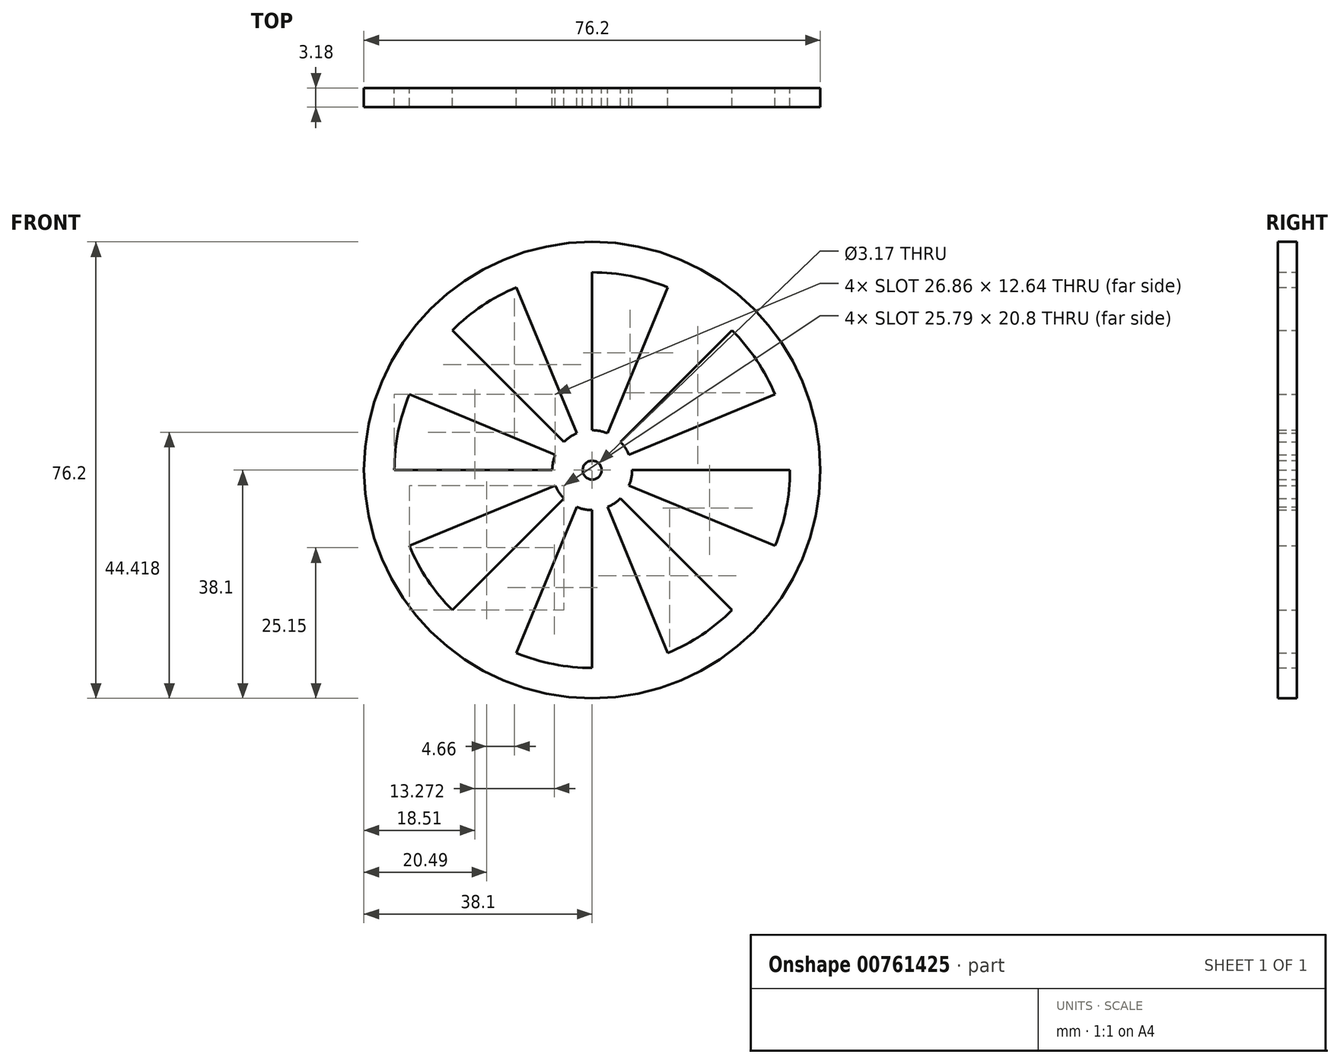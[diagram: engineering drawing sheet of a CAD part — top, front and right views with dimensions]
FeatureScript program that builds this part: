
annotation { "Feature Type Name" : "Feature", "Feature Type Description" : "" }
export const myFeature = defineFeature(function(context is Context, id is Id, definition is map)
    precondition{}
    {
        {
            var Q0;
            Q0=qCreatedBy(makeId("Front.planeOp"),FACE);
            var sketch = newSketch(context, id + "F0", { "sketchPlane" : qUnion([Q0])});
            skCircle(sketch, "E0", {"center": v(0, 0) * mm, "radius": 38.1 * mm});
            skCircle(sketch, "E1", {"center": v(0, 0) * mm, "radius": 33.02 * mm});
            skCircle(sketch, "E2", {"center": v(0, 0) * mm, "radius": 1.59 * mm});
            skCircle(sketch, "E3", {"center": v(0, 0) * mm, "radius": 6.67 * mm});
            skLineSegment(sketch, "E4", {"start": v(0, -33.02) * mm, "end": v(0, -6.67) * mm});
            skLineSegment(sketch, "E5", {"start": v(-12.64, -30.5) * mm, "end": v(-2.55, -6.16) * mm});
            skLineSegment(sketch, "E6.1.0", {"start": v(12.64, -30.5) * mm, "end": v(2.55, -6.16) * mm});
            skLineSegment(sketch, "E6.1.1", {"start": v(23.35, -23.35) * mm, "end": v(4.71, -4.71) * mm});
            skLineSegment(sketch, "E6.2.0", {"start": v(30.5, -12.64) * mm, "end": v(6.16, -2.55) * mm});
            skLineSegment(sketch, "E6.2.1", {"start": v(33.02, 0) * mm, "end": v(6.67, 0) * mm});
            skLineSegment(sketch, "E6.3.0", {"start": v(30.5, 12.64) * mm, "end": v(6.16, 2.55) * mm});
            skLineSegment(sketch, "E6.3.1", {"start": v(23.35, 23.35) * mm, "end": v(4.71, 4.71) * mm});
            skLineSegment(sketch, "E6.4.0", {"start": v(12.64, 30.5) * mm, "end": v(2.55, 6.16) * mm});
            skLineSegment(sketch, "E6.4.1", {"start": v(0, 33.02) * mm, "end": v(0, 6.67) * mm});
            skLineSegment(sketch, "E6.5.0", {"start": v(-12.64, 30.5) * mm, "end": v(-2.55, 6.16) * mm});
            skLineSegment(sketch, "E6.5.1", {"start": v(-23.35, 23.35) * mm, "end": v(-4.71, 4.71) * mm});
            skLineSegment(sketch, "E6.6.0", {"start": v(-30.5, 12.64) * mm, "end": v(-6.16, 2.55) * mm});
            skLineSegment(sketch, "E6.6.1", {"start": v(-33.02, 0) * mm, "end": v(-6.67, 0) * mm});
            skLineSegment(sketch, "E6.7.0", {"start": v(-30.5, -12.64) * mm, "end": v(-6.16, -2.55) * mm});
            skLineSegment(sketch, "E6.7.1", {"start": v(-23.35, -23.35) * mm, "end": v(-4.71, -4.71) * mm});
            skSolve(sketch);
        }
        {
            var Q0;
            Q0 = qSketchRegion(id + "F0", true);
            var Q1;
            Q1=makeQuery(id+"F0.imprint","IMPRINT",FACE,{"disambiguationData":[TD([[makeQuery(id+"F0.imprint","IMPRINT",EDGE,{"derivedFrom":sQuery(id+"F0.wireOp",EDGE,"E2")}),-1.0]])]});
            var Q2;
            {var subQ0=sQuery(id+"F0.wireOp",EDGE,"lldFvJbT-TWuF-h2Xa-A9au-xammMzHIPNwq");Q2=makeQuery(id+"F0.imprint","IMPRINT",FACE,{"disambiguationData":[TD([[makeQuery(id+"F0.imprint","IMPRINT",EDGE,{"derivedFrom":subQ0}),-1.0]])]});}
            var Q3;
            {var subQ0=sQuery(id+"F0.wireOp",EDGE,"715rP11S-6pFs-39Mx-Qieq-1ZQKDfbsE7nD");Q3=makeQuery(id+"F0.imprint","IMPRINT",FACE,{"disambiguationData":[TD([[makeQuery(id+"F0.imprint","IMPRINT",EDGE,{"derivedFrom":subQ0}),-1.0]])]});}
            var Q4;
            {var subQ0=sQuery(id+"F0.wireOp",EDGE,"qHrydl03-OtEe-SUIx-3vZ6-cvQDLL1FTTK6");Q4=makeQuery(id+"F0.imprint","IMPRINT",FACE,{"disambiguationData":[TD([[makeQuery(id+"F0.imprint","IMPRINT",EDGE,{"derivedFrom":subQ0}),1.0]])]});}
            var Q5;
            {var subQ0=sQuery(id+"F0.wireOp",EDGE,"oGSza807-AtUG-UJ8H-9Y2e-SBF4vyUKvPuy");Q5=makeQuery(id+"F0.imprint","IMPRINT",FACE,{"disambiguationData":[TD([[makeQuery(id+"F0.imprint","IMPRINT",EDGE,{"derivedFrom":subQ0}),1.0]])]});}
            var Q6;
            {var subQ0=sQuery(id+"F0.wireOp",EDGE,"4UbqkdUl-KGWa-6nsk-hcE0-c5eqDtJH95Mi");Q6=makeQuery(id+"F0.imprint","IMPRINT",FACE,{"disambiguationData":[TD([[makeQuery(id+"F0.imprint","IMPRINT",EDGE,{"derivedFrom":subQ0}),1.0]])]});}
            var Q7;
            {var subQ0=sQuery(id+"F0.wireOp",EDGE,"E4");Q7=makeQuery(id+"F0.imprint","IMPRINT",FACE,{"disambiguationData":[TD([[makeQuery(id+"F0.imprint","IMPRINT",EDGE,{"derivedFrom":subQ0}),-1.0]])]});}
            var Q8;
            {var subQ0=sQuery(id+"F0.wireOp",EDGE,"8IWaelDn-k7BH-PMnv-vkTP-gdRP4jC8m3hk");Q8=makeQuery(id+"F0.imprint","IMPRINT",FACE,{"disambiguationData":[TD([[makeQuery(id+"F0.imprint","IMPRINT",EDGE,{"derivedFrom":subQ0}),-1.0]])]});}
            var Q9;
            {var subQ0=sQuery(id+"F0.wireOp",EDGE,"pzI2Y8JE-G3gC-hC4l-CGai-oNIetJQlt4ru");Q9=makeQuery(id+"F0.imprint","IMPRINT",FACE,{"disambiguationData":[TD([[makeQuery(id+"F0.imprint","IMPRINT",EDGE,{"derivedFrom":subQ0}),1.0]])]});}
            extrude(context, id + "F1", {"entities" : qUnion([Q0, Q1, Q2, Q3, Q4, Q5, Q6, Q7, Q8, Q9]), "depth" : 3.17 * mm, "offsetDistance" : 25.4 * mm});
        }
        {
            var Q0;
            Q0 = qSketchRegion(id + "F0", true);
            var Q1;
            {var subQ0=sQuery(id+"F0.wireOp",EDGE,"E5");Q1=makeQuery(id+"F0.imprint","IMPRINT",FACE,{"disambiguationData":[TD([[makeQuery(id+"F0.imprint","IMPRINT",EDGE,{"derivedFrom":subQ0}),1.0]])]});}
            var Q2;
            {var subQ0=sQuery(id+"F0.wireOp",EDGE,"E6.6.1");Q2=makeQuery(id+"F0.imprint","IMPRINT",FACE,{"disambiguationData":[TD([[makeQuery(id+"F0.imprint","IMPRINT",EDGE,{"derivedFrom":subQ0}),-1.0]])]});}
            var Q3;
            {var subQ0=sQuery(id+"F0.wireOp",EDGE,"E6.5.1");Q3=makeQuery(id+"F0.imprint","IMPRINT",FACE,{"disambiguationData":[TD([[makeQuery(id+"F0.imprint","IMPRINT",EDGE,{"derivedFrom":subQ0}),-1.0]])]});}
            var Q4;
            {var subQ0=sQuery(id+"F0.wireOp",EDGE,"E6.4.1");Q4=makeQuery(id+"F0.imprint","IMPRINT",FACE,{"disambiguationData":[TD([[makeQuery(id+"F0.imprint","IMPRINT",EDGE,{"derivedFrom":subQ0}),-1.0]])]});}
            var Q5;
            {var subQ0=sQuery(id+"F0.wireOp",EDGE,"E6.3.1");Q5=makeQuery(id+"F0.imprint","IMPRINT",FACE,{"disambiguationData":[TD([[makeQuery(id+"F0.imprint","IMPRINT",EDGE,{"derivedFrom":subQ0}),-1.0]])]});}
            var Q6;
            {var subQ0=sQuery(id+"F0.wireOp",EDGE,"E6.2.1");Q6=makeQuery(id+"F0.imprint","IMPRINT",FACE,{"disambiguationData":[TD([[makeQuery(id+"F0.imprint","IMPRINT",EDGE,{"derivedFrom":subQ0}),-1.0]])]});}
            var Q7;
            {var subQ0=sQuery(id+"F0.wireOp",EDGE,"E6.1.1");Q7=makeQuery(id+"F0.imprint","IMPRINT",FACE,{"disambiguationData":[TD([[makeQuery(id+"F0.imprint","IMPRINT",EDGE,{"derivedFrom":subQ0}),-1.0]])]});}
            extrude(context, id + "F2", {"entities" : qUnion([Q0, Q1, Q2, Q3, Q4, Q5, Q6, Q7]), "operationType" : NewBodyOperationType.ADD, "depth" : 3.17 * mm, "offsetDistance" : 25.4 * mm});
        }
    });
